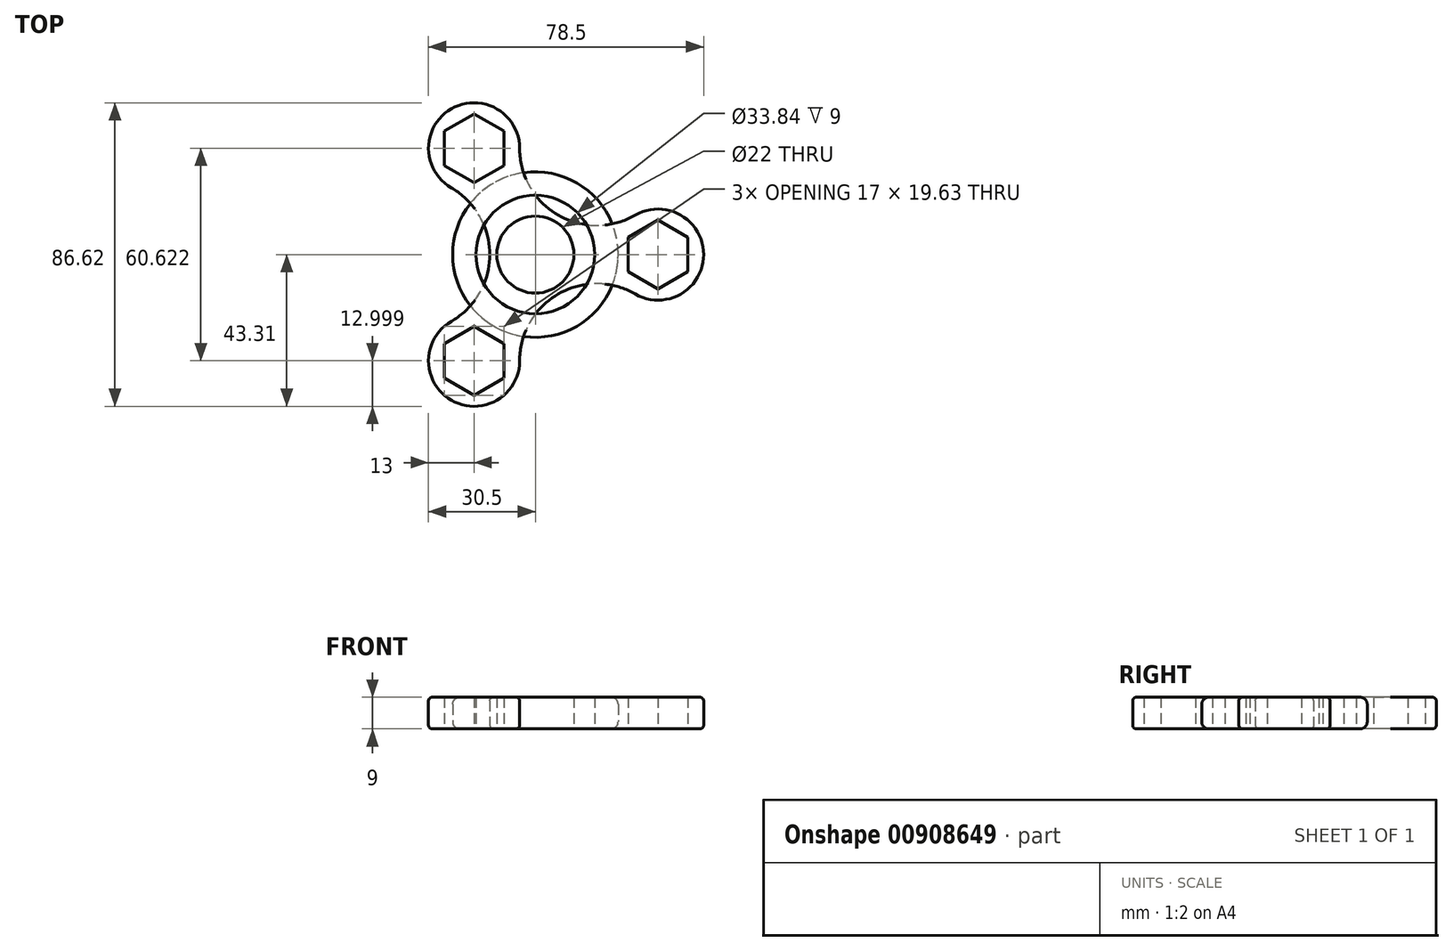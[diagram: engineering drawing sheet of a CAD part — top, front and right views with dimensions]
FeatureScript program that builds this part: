
annotation { "Feature Type Name" : "Feature", "Feature Type Description" : "" }
export const myFeature = defineFeature(function(context is Context, id is Id, definition is map)
    precondition{}
    {
        {
            var Q0;
            Q0=qCreatedBy(makeId("Top.planeOp"),FACE);
            var sketch = newSketch(context, id + "F0", { "sketchPlane" : qUnion([Q0])});
            skLineSegment(sketch, "E0", {"start": v(0, 0) * mm, "end": v(35, 0) * mm});
            skLineSegment(sketch, "E1", {"start": v(0, 0) * mm, "end": v(-17.5, 30.31) * mm});
            skLineSegment(sketch, "E2", {"start": v(0, 0) * mm, "end": v(-17.5, -30.31) * mm});
            skCircle(sketch, "E3", {"center": v(-17.5, 30.31) * mm, "radius": 11 * mm});
            skCircle(sketch, "E4", {"center": v(35, 0) * mm, "radius": 11 * mm});
            skCircle(sketch, "E5", {"center": v(-17.5, -30.31) * mm, "radius": 11 * mm});
            skCircle(sketch, "E6", {"center": v(0, 0) * mm, "radius": 11 * mm});
            skLineSegment(sketch, "E7", {"start": v(0, 0) * mm, "end": v(17.5, 30.31) * mm});
            skLineSegment(sketch, "E8", {"start": v(0, 0) * mm, "end": v(17.5, -30.31) * mm});
            skLineSegment(sketch, "E9", {"start": v(0, 0) * mm, "end": v(-35, 0) * mm});
            skCircle(sketch, "E10", {"center": v(35, 0) * mm, "radius": 13 * mm});
            skCircle(sketch, "E11", {"center": v(-17.5, -30.31) * mm, "radius": 13 * mm});
            skCircle(sketch, "E12", {"center": v(-17.5, 30.31) * mm, "radius": 13 * mm});
            skArc(sketch, "E13", {"start": v(-4.5, 30.31) * mm, "mid": v(6.5, 11.26) * mm, "end": v(28.5, 11.26) * mm});
            skArc(sketch, "E14", {"start": v(-24, -19.05) * mm, "mid": v(-13, 0) * mm, "end": v(-24, 19.05) * mm});
            skArc(sketch, "E15", {"start": v(28.5, -11.26) * mm, "mid": v(6.5, -11.26) * mm, "end": v(-4.5, -30.31) * mm});
            skCircle(sketch, "E16.cCircle", {"center": v(-17.5, 30.31) * mm, "radius": 8.5 * mm, "construction": true});
            skLineSegment(sketch, "E16.0", {"start": v(-9, 25.4) * mm, "end": v(-17.5, 20.5) * mm});
            skLineSegment(sketch, "E16.1", {"start": v(-17.5, 20.5) * mm, "end": v(-26, 25.4) * mm});
            skLineSegment(sketch, "E16.2", {"start": v(-26, 25.4) * mm, "end": v(-26, 35.22) * mm});
            skLineSegment(sketch, "E16.3", {"start": v(-26, 35.22) * mm, "end": v(-17.5, 40.13) * mm});
            skLineSegment(sketch, "E16.4", {"start": v(-17.5, 40.13) * mm, "end": v(-9, 35.22) * mm});
            skLineSegment(sketch, "E16.5", {"start": v(-9, 35.22) * mm, "end": v(-9, 25.4) * mm});
            skPoint(sketch, "E16.0.midPoint", {"position": v(-13.25, 22.95) * mm});
            skCircle(sketch, "E17.cCircle", {"center": v(35, 0) * mm, "radius": 8.5 * mm, "construction": true});
            skLineSegment(sketch, "E17.0", {"start": v(26.5, -4.9) * mm, "end": v(26.5, 4.9) * mm});
            skLineSegment(sketch, "E17.1", {"start": v(26.5, 4.9) * mm, "end": v(35, 9.81) * mm});
            skLineSegment(sketch, "E17.2", {"start": v(35, 9.81) * mm, "end": v(43.5, 4.9) * mm});
            skLineSegment(sketch, "E17.3", {"start": v(43.5, 4.9) * mm, "end": v(43.5, -4.9) * mm});
            skLineSegment(sketch, "E17.4", {"start": v(43.5, -4.9) * mm, "end": v(35, -9.81) * mm});
            skLineSegment(sketch, "E17.5", {"start": v(35, -9.81) * mm, "end": v(26.5, -4.9) * mm});
            skPoint(sketch, "E17.0.midPoint", {"position": v(26.5, 0) * mm});
            skCircle(sketch, "E18.cCircle", {"center": v(-17.5, -30.31) * mm, "radius": 8.5 * mm, "construction": true});
            skLineSegment(sketch, "E18.0", {"start": v(-17.5, -40.13) * mm, "end": v(-26, -35.22) * mm});
            skLineSegment(sketch, "E18.1", {"start": v(-26, -35.22) * mm, "end": v(-26, -25.4) * mm});
            skLineSegment(sketch, "E18.2", {"start": v(-26, -25.4) * mm, "end": v(-17.5, -20.5) * mm});
            skLineSegment(sketch, "E18.3", {"start": v(-17.5, -20.5) * mm, "end": v(-9, -25.4) * mm});
            skLineSegment(sketch, "E18.4", {"start": v(-9, -25.4) * mm, "end": v(-9, -35.22) * mm});
            skLineSegment(sketch, "E18.5", {"start": v(-9, -35.22) * mm, "end": v(-17.5, -40.13) * mm});
            skPoint(sketch, "E18.0.midPoint", {"position": v(-21.75, -37.67) * mm});
            skSolve(sketch);
        }
        {
            var Q0;
            {var subQ5=sQuery(id+"F0.wireOp",EDGE,"E1");var subQ7=sQuery(id+"F0.wireOp",EDGE,"E12");var subQ9=makeQuery(id+"F0.imprint","INTERSECT",VERTEX,{"derivedFrom":[subQ5,subQ7]});Q0=makeQuery(id+"F0.imprint","IMPRINT",FACE,{"disambiguationData":[TD([[makeQuery(id+"F0.imprint","IMPRINT",EDGE,{"disambiguationData":[TD([[subQ9,1.0]])],"derivedFrom":subQ5}),1.0]])]});}
            var Q1;
            {var subQ1=sQuery(id+"F0.wireOp",EDGE,"E12");var subQ3=sQuery(id+"F0.wireOp",EDGE,"E1");var subQ4=makeQuery(id+"F0.imprint","INTERSECT",VERTEX,{"derivedFrom":[subQ3,subQ1]});Q1=makeQuery(id+"F0.imprint","IMPRINT",FACE,{"disambiguationData":[TD([[makeQuery(id+"F0.imprint","IMPRINT",EDGE,{"disambiguationData":[TD([[subQ4,1.0]])],"derivedFrom":subQ3}),-1.0]])]});}
            var Q2;
            {var subQ1=sQuery(id+"F0.wireOp",EDGE,"E0");var subQ6=sQuery(id+"F0.wireOp",EDGE,"E10");var subQ9=makeQuery(id+"F0.imprint","INTERSECT",VERTEX,{"derivedFrom":[subQ1,subQ6]});Q2=makeQuery(id+"F0.imprint","IMPRINT",FACE,{"disambiguationData":[TD([[makeQuery(id+"F0.imprint","IMPRINT",EDGE,{"disambiguationData":[TD([[subQ9,1.0]])],"derivedFrom":subQ1}),1.0]])]});}
            var Q3;
            {var subQ1=sQuery(id+"F0.wireOp",EDGE,"E10");var subQ3=sQuery(id+"F0.wireOp",EDGE,"E0");var subQ4=makeQuery(id+"F0.imprint","INTERSECT",VERTEX,{"derivedFrom":[subQ3,subQ1]});Q3=makeQuery(id+"F0.imprint","IMPRINT",FACE,{"disambiguationData":[TD([[makeQuery(id+"F0.imprint","IMPRINT",EDGE,{"disambiguationData":[TD([[subQ4,1.0]])],"derivedFrom":subQ3}),-1.0]])]});}
            var Q4;
            {var subQ1=sQuery(id+"F0.wireOp",EDGE,"E11");var subQ3=sQuery(id+"F0.wireOp",EDGE,"E2");var subQ4=makeQuery(id+"F0.imprint","INTERSECT",VERTEX,{"derivedFrom":[subQ3,subQ1]});Q4=makeQuery(id+"F0.imprint","IMPRINT",FACE,{"disambiguationData":[TD([[makeQuery(id+"F0.imprint","IMPRINT",EDGE,{"disambiguationData":[TD([[subQ4,1.0]])],"derivedFrom":subQ3}),1.0]])]});}
            var Q5;
            {var subQ1=sQuery(id+"F0.wireOp",EDGE,"E2");var subQ6=sQuery(id+"F0.wireOp",EDGE,"E11");var subQ8=makeQuery(id+"F0.imprint","INTERSECT",VERTEX,{"derivedFrom":[subQ1,subQ6]});Q5=makeQuery(id+"F0.imprint","IMPRINT",FACE,{"disambiguationData":[TD([[makeQuery(id+"F0.imprint","IMPRINT",EDGE,{"disambiguationData":[TD([[subQ8,1.0]])],"derivedFrom":subQ1}),-1.0]])]});}
            var Q6;
            Q6=makeQuery(id+"F0.imprint","IMPRINT",FACE,{"disambiguationData":[TD([[makeQuery(id+"F0.imprint","IMPRINT",EDGE,{"derivedFrom":sQuery(id+"F0.wireOp",EDGE,"E4")}),-1.0]])]});
            var Q7;
            Q7=makeQuery(id+"F0.imprint","IMPRINT",FACE,{"disambiguationData":[TD([[makeQuery(id+"F0.imprint","IMPRINT",EDGE,{"derivedFrom":sQuery(id+"F0.wireOp",EDGE,"E3")}),-1.0]])]});
            var Q8;
            Q8=makeQuery(id+"F0.imprint","IMPRINT",FACE,{"disambiguationData":[TD([[makeQuery(id+"F0.imprint","IMPRINT",EDGE,{"derivedFrom":sQuery(id+"F0.wireOp",EDGE,"E5")}),-1.0]])]});
            extrude(context, id + "F1", {"entities" : qUnion([Q0, Q1, Q2, Q3, Q4, Q5, Q6, Q7, Q8]), "endBound" : BoundingType.SYMMETRIC, "depth" : 9 * mm, "offsetDistance" : 25 * mm});
        }
        {
            var Q0;
            Q0=makeQuery(id+"F1.opExtrude","CAP_EDGE",EDGE,{"disambiguationData":[OSD([sQuery(id+"F0.wireOp",EDGE,"E15")])],"isStart":false});
            var Q1;
            Q1=makeQuery(id+"F1.opExtrude","CAP_EDGE",EDGE,{"disambiguationData":[OSD([sQuery(id+"F0.wireOp",EDGE,"E13")])],"isStart":true});
            var Q2;
            Q2=makeQuery(id+"F1.opExtrude","CAP_EDGE",EDGE,{"disambiguationData":[OSD([sQuery(id+"F0.wireOp",EDGE,"E14")])],"isStart":true});
            fillet(context, id + "F2", {"entities" : qUnion([Q0, Q1, Q2]), "radius" : 1 * mm, "tangentPropagation" : true, "allowEdgeOverflow" : false});
        }
        {
            var Q0;
            Q0=makeQuery(id+"F0.imprint","IMPRINT",FACE,{"disambiguationData":[TD([[makeQuery(id+"F0.imprint","IMPRINT",EDGE,{"derivedFrom":sQuery(id+"F0.wireOp",EDGE,"E3")}),1.0]])]});
            var Q1;
            Q1=makeQuery(id+"F0.imprint","IMPRINT",FACE,{"disambiguationData":[TD([[makeQuery(id+"F0.imprint","IMPRINT",EDGE,{"derivedFrom":sQuery(id+"F0.wireOp",EDGE,"E4")}),1.0]])]});
            var Q2;
            Q2=makeQuery(id+"F0.imprint","IMPRINT",FACE,{"disambiguationData":[TD([[makeQuery(id+"F0.imprint","IMPRINT",EDGE,{"derivedFrom":sQuery(id+"F0.wireOp",EDGE,"E5")}),1.0]])]});
            extrude(context, id + "F3", {"entities" : qUnion([Q0, Q1, Q2]), "operationType" : NewBodyOperationType.ADD, "depth" : 4.5 * mm, "offsetDistance" : 25 * mm});
        }
        {
            var Q0;
            Q0=qCreatedBy(makeId("Top.planeOp"),FACE);
            var sketch = newSketch(context, id + "F4", { "sketchPlane" : qUnion([Q0])});
            skCircle(sketch, "E19", {"center": v(0, 0) * mm, "radius": 16.92 * mm});
            skCircle(sketch, "E20", {"center": v(0, 0) * mm, "radius": 23.61 * mm});
            skSolve(sketch);
        }
        {
            var Q0;
            Q0=makeQuery(id+"F4.imprint","IMPRINT",FACE,{"disambiguationData":[TD([[makeQuery(id+"F4.imprint","IMPRINT",EDGE,{"derivedFrom":sQuery(id+"F4.wireOp",EDGE,"E19")}),-1.0]])]});
            extrude(context, id + "F5", {"entities" : qUnion([Q0]), "endBound" : BoundingType.SYMMETRIC, "depth" : 9 * mm, "offsetDistance" : 25 * mm});
        }
        {
            var Q0;
            Q0=makeQuery(id+"F0.imprint","IMPRINT",FACE,{"disambiguationData":[TD([[makeQuery(id+"F0.imprint","IMPRINT",EDGE,{"derivedFrom":sQuery(id+"F0.wireOp",EDGE,"E4")}),1.0]])]});
            var Q1;
            Q1=makeQuery(id+"F0.imprint","IMPRINT",FACE,{"disambiguationData":[TD([[makeQuery(id+"F0.imprint","IMPRINT",EDGE,{"derivedFrom":sQuery(id+"F0.wireOp",EDGE,"E3")}),1.0]])]});
            var Q2;
            Q2=makeQuery(id+"F0.imprint","IMPRINT",FACE,{"disambiguationData":[TD([[makeQuery(id+"F0.imprint","IMPRINT",EDGE,{"derivedFrom":sQuery(id+"F0.wireOp",EDGE,"E5")}),1.0]])]});
            extrude(context, id + "F6", {"entities" : qUnion([Q0, Q1, Q2]), "operationType" : NewBodyOperationType.ADD, "oppositeDirection" : true, "depth" : 4.5 * mm, "offsetDistance" : 25 * mm});
        }
        {
            var Q0;
            Q0=makeQuery(id+"F5.opExtrude","CAP_EDGE",EDGE,{"disambiguationData":[OSD([sQuery(id+"F4.wireOp",EDGE,"E20")])],"isStart":false});
            var Q1;
            Q1=makeQuery(id+"F5.opExtrude","CAP_EDGE",EDGE,{"disambiguationData":[OSD([sQuery(id+"F4.wireOp",EDGE,"E20")])],"isStart":true});
            fillet(context, id + "F7", {"entities" : qUnion([Q0, Q1]), "radius" : 2 * mm, "tangentPropagation" : true, "allowEdgeOverflow" : false});
        }
    });
